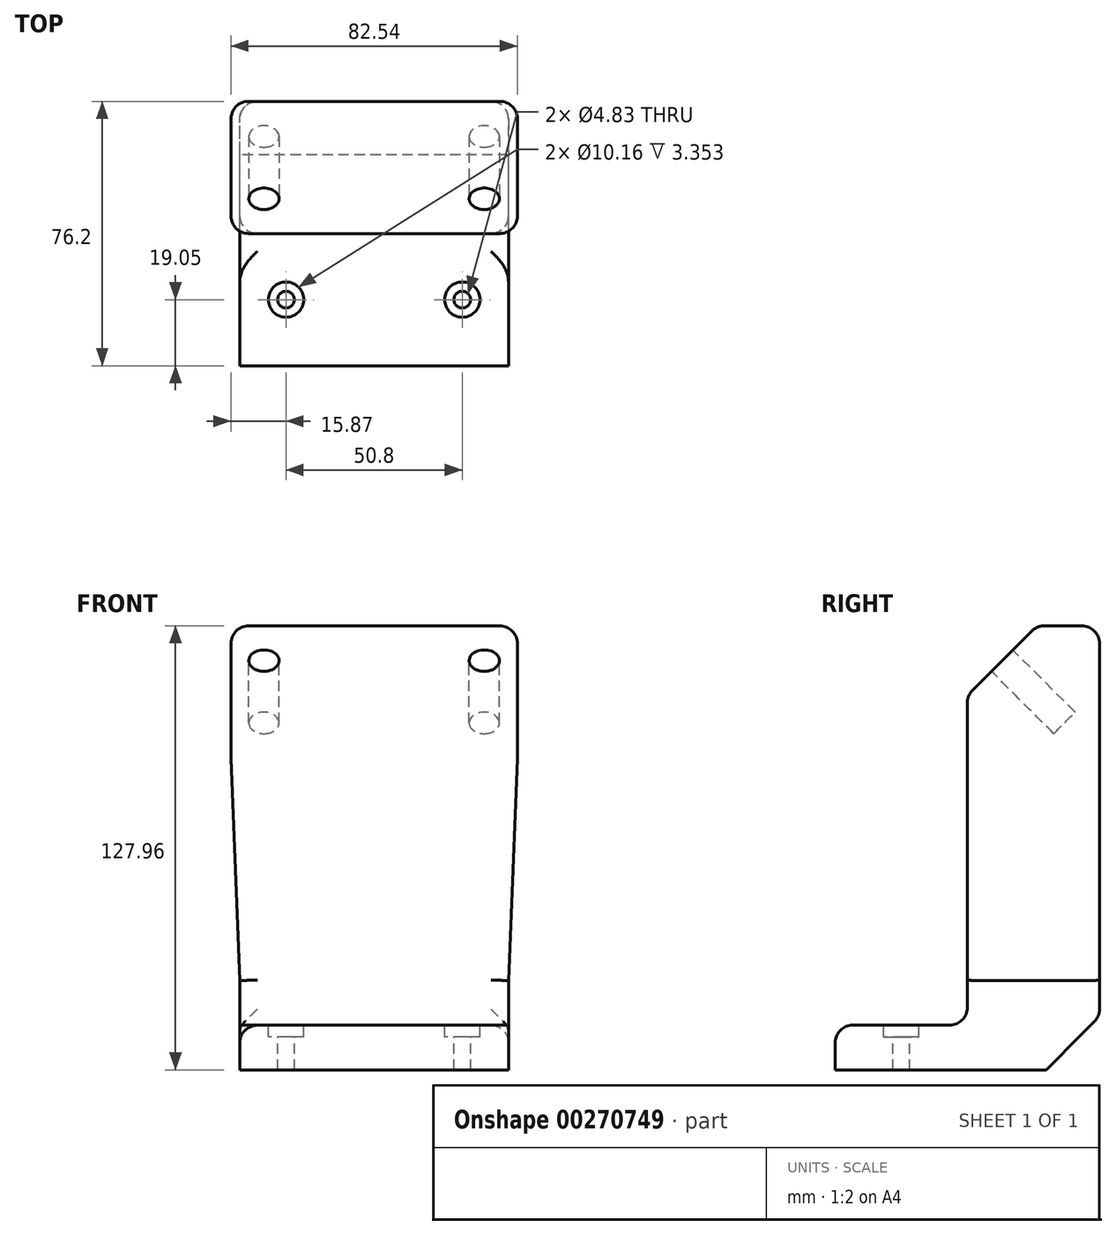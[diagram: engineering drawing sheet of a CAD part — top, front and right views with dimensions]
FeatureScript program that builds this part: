
annotation { "Feature Type Name" : "Feature", "Feature Type Description" : "" }
export const myFeature = defineFeature(function(context is Context, id is Id, definition is map)
    precondition{}
    {
        {
            var Q0;
            Q0=qCreatedBy(makeId("Front.planeOp"),FACE);
            var sketch = newSketch(context, id + "F0", { "sketchPlane" : qUnion([Q0])});
            skLineSegment(sketch, "E0.top", {"start": v(0, -76.68) * mm, "end": v(-38.71, -76.68) * mm});
            skLineSegment(sketch, "E0.left", {"start": v(41.28, 51.28) * mm, "end": v(41.28, 13.06) * mm});
            skLineSegment(sketch, "E0.right", {"start": v(-41.27, 51.28) * mm, "end": v(-41.28, 13.06) * mm});
            skPoint(sketch, "E0.middle", {"position": v(0, 0) * mm});
            skLineSegment(sketch, "E1", {"start": v(-38.74, -50.4) * mm, "end": v(-41.28, 13.06) * mm});
            skPoint(sketch, "E2.endSnap0", {"position": v(0, -76.68) * mm});
            skPoint(sketch, "E3.orphan", {"position": v(-41.28, -76.68) * mm});
            skPoint(sketch, "E2.end.orphan", {"position": v(0, -57.6) * mm});
            skPoint(sketch, "E2.start.orphan", {"position": v(0, -76.68) * mm});
            skPoint(sketch, "E4.orphan", {"position": v(41.28, -76.68) * mm});
            skLineSegment(sketch, "E5", {"start": v(-41.27, 13.06) * mm, "end": v(-38.71, -50.93) * mm});
            skLineSegment(sketch, "E6", {"start": v(-38.71, -50.93) * mm, "end": v(-38.71, -76.68) * mm});
            skLineSegment(sketch, "E7", {"start": v(0, -76.68) * mm, "end": v(0, -57.6) * mm});
            skLineSegment(sketch, "E8.MirrorCS", {"start": v(0, -76.68) * mm, "end": v(38.71, -76.68) * mm});
            skLineSegment(sketch, "E9.MirrorCS", {"start": v(38.71, -50.93) * mm, "end": v(38.71, -76.68) * mm});
            skLineSegment(sketch, "E10.MirrorCS", {"start": v(41.28, 13.06) * mm, "end": v(38.71, -50.93) * mm});
            skPoint(sketch, "E0.bottom.end.orphan", {"position": v(-41.27, 76.68) * mm});
            skPoint(sketch, "E11.orphan", {"position": v(41.28, 76.68) * mm});
            skLineSegment(sketch, "E12", {"start": v(41.28, 51.28) * mm, "end": v(-41.28, 51.28) * mm});
            skSolve(sketch);
        }
        {
            var Q0;
            Q0 = qSketchRegion(id + "F0", true);
            extrude(context, id + "F1", {"entities" : qUnion([Q0]), "depth" : 38.1 * mm});
        }
        {
            var Q0;
            Q0=makeQuery(id+"F1.opExtrude","SWEPT_FACE",FACE,{"disambiguationData":[OSD([sQuery(id+"F0.wireOp",EDGE,"E0.left")])]});
            var sketch = newSketch(context, id + "F2", { "sketchPlane" : qUnion([Q0])});
            skLineSegment(sketch, "E13", {"start": v(-18.08, 51.28) * mm, "end": v(-38.1, 51.28) * mm});
            skLineSegment(sketch, "E14", {"start": v(-38.1, 51.28) * mm, "end": v(-38.1, 31.27) * mm});
            skLineSegment(sketch, "E15", {"start": v(-18.08, 51.28) * mm, "end": v(-38.1, 31.27) * mm});
            skSolve(sketch);
        }
        {
            var Q0;
            Q0 = qSketchRegion(id + "F2", true);
            extrude(context, id + "F3", {"entities" : qUnion([Q0]), "operationType" : NewBodyOperationType.REMOVE, "oppositeDirection" : true, "depth" : 127 * mm});
        }
        {
            var Q0;
            Q0=makeQuery(id+"F3.boolean.opBoolean","COPY",FACE,{"derivedFrom":makeQuery(id+"F3.opExtrude","SWEPT_FACE",FACE,{"disambiguationData":[OSD([sQuery(id+"F2.wireOp",EDGE,"E15")])]})});
            var sketch = newSketch(context, id + "F4", { "sketchPlane" : qUnion([Q0])});
            skPoint(sketch, "E16", {"position": v(-31.75, 18.3) * mm});
            skPoint(sketch, "E17", {"position": v(31.75, 18.3) * mm});
            skPoint(sketch, "E18", {"position": v(-31.75, 9.32) * mm});
            skPoint(sketch, "E18.positionSnap0", {"position": v(-41.28, 9.32) * mm});
            skPoint(sketch, "E19", {"position": v(31.75, 9.32) * mm});
            skCircle(sketch, "E20", {"center": v(-31.75, 9.32) * mm, "radius": 4.37 * mm});
            skCircle(sketch, "E21", {"center": v(31.75, 9.32) * mm, "radius": 4.37 * mm});
            skSolve(sketch);
        }
        {
            var Q0;
            Q0 = qSketchRegion(id + "F4", true);
            extrude(context, id + "F5", {"entities" : qUnion([Q0]), "operationType" : NewBodyOperationType.REMOVE, "oppositeDirection" : true, "depth" : 25.4 * mm});
        }
        {
            var Q0;
            Q0=makeQuery(id+"F1.opExtrude","CAP_FACE",FACE,{"disambiguationData":[OSD([sQuery(id+"F0.wireOp",EDGE,"E0.bottom"),sQuery(id+"F0.wireOp",EDGE,"E0.top"),sQuery(id+"F0.wireOp",EDGE,"E0.left"),sQuery(id+"F0.wireOp",EDGE,"E0.right"),sQuery(id+"F0.wireOp",EDGE,"E5"),sQuery(id+"F0.wireOp",EDGE,"E6"),sQuery(id+"F0.wireOp",EDGE,"E8.MirrorCS"),sQuery(id+"F0.wireOp",EDGE,"E9.MirrorCS"),sQuery(id+"F0.wireOp",EDGE,"E10.MirrorCS")])],"isStart":false});
            var sketch = newSketch(context, id + "F6", { "sketchPlane" : qUnion([Q0])});
            skLineSegment(sketch, "E22.bottom", {"start": v(38.71, -76.68) * mm, "end": v(-38.71, -76.68) * mm});
            skLineSegment(sketch, "E22.left", {"start": v(38.71, -76.68) * mm, "end": v(38.71, -63.8) * mm});
            skLineSegment(sketch, "E22.right", {"start": v(-38.71, -76.68) * mm, "end": v(-38.71, -63.8) * mm});
            skPoint(sketch, "E22.middle", {"position": v(0, -67.48) * mm});
            skPoint(sketch, "E22.middle.positionSnap0", {"position": v(0, -76.68) * mm});
            skPoint(sketch, "E22.centerSnap0", {"position": v(0, -76.68) * mm});
            skLineSegment(sketch, "E23", {"start": v(-38.71, -63.8) * mm, "end": v(38.71, -63.8) * mm});
            skPoint(sketch, "E24.orphan", {"position": v(38.71, -58.28) * mm});
            skPoint(sketch, "E25.orphan", {"position": v(-38.71, -58.28) * mm});
            skSolve(sketch);
        }
        {
            var Q0;
            Q0 = qSketchRegion(id + "F6", true);
            extrude(context, id + "F7", {"entities" : qUnion([Q0]), "operationType" : NewBodyOperationType.ADD, "depth" : 38.1 * mm});
        }
        {
            var Q0;
            Q0=makeQuery(id+"F7.opExtrude","SWEPT_FACE",FACE,{"disambiguationData":[OSD([sQuery(id+"F6.wireOp",EDGE,"E23")])]});
            var sketch = newSketch(context, id + "F8", { "sketchPlane" : qUnion([Q0])});
            skLineSegment(sketch, "E26", {"start": v(0, -57.15) * mm, "end": v(-25.4, -57.15) * mm});
            skPoint(sketch, "E26.startSnap0", {"position": v(-38.71, -57.15) * mm});
            skPoint(sketch, "E26.endSnap0", {"position": v(38.71, -57.15) * mm});
            skLineSegment(sketch, "E27", {"start": v(-25.4, -57.15) * mm, "end": v(25.4, -57.15) * mm});
            skPoint(sketch, "E28", {"position": v(-25.4, -57.15) * mm});
            skPoint(sketch, "E29", {"position": v(25.4, -57.15) * mm});
            skSolve(sketch);
        }
        {
            var Q0;
            Q0=sQuery(id+"F8.wireOp",VERTEX,"E28");
            var Q1;
            Q1=sQuery(id+"F8.wireOp",VERTEX,"E29");
            var Q2;
            Q2=makeQuery(id+"F1.opExtrude","SWEPT_BODY",BODY,{"disambiguationData":[OSD([sQuery(id+"F0.wireOp",EDGE,"E0.bottom"),sQuery(id+"F0.wireOp",EDGE,"E0.top"),sQuery(id+"F0.wireOp",EDGE,"E0.left"),sQuery(id+"F0.wireOp",EDGE,"E0.right"),sQuery(id+"F0.wireOp",EDGE,"E5"),sQuery(id+"F0.wireOp",EDGE,"E6"),sQuery(id+"F0.wireOp",EDGE,"E8.MirrorCS"),sQuery(id+"F0.wireOp",EDGE,"E9.MirrorCS"),sQuery(id+"F0.wireOp",EDGE,"E10.MirrorCS")])]});
            hole(context, id + "F9", {"style" : HoleStyle.C_BORE, "endStyle" : HoleEndStyle.THROUGH, "holeDiameter" : 4.83 * mm, "cBoreDiameter" : 10.16 * mm, "cBoreDepth" : 3.35 * mm, "tappedDepth" : 12.7 * mm, "tapClearance" : 3, "locations" : qUnion([Q0, Q1]), "scope" : qUnion([Q2])});
        }
        {
            var Q0;
            Q0=makeQuery(id+"F7.boolean.opBoolean","MERGE",FACE,{"derivedFrom":[makeQuery(id+"F1.opExtrude","SWEPT_FACE",FACE,{"disambiguationData":[OSD([sQuery(id+"F0.wireOp",EDGE,"E6")])]}),makeQuery(id+"F7.opExtrude","SWEPT_FACE",FACE,{"disambiguationData":[OSD([sQuery(id+"F6.wireOp",EDGE,"E22.right")])]})]});
            var sketch = newSketch(context, id + "F10", { "sketchPlane" : qUnion([Q0])});
            skLineSegment(sketch, "E30", {"start": v(0, -76.68) * mm, "end": v(0, -63.8) * mm});
            skLineSegment(sketch, "E31", {"start": v(0, -76.68) * mm, "end": v(12.88, -76.68) * mm});
            skLineSegment(sketch, "E32", {"start": v(12.88, -76.68) * mm, "end": v(0, -63.8) * mm});
            skSolve(sketch);
        }
        {
            var Q0;
            Q0 = qSketchRegion(id + "F10", true);
            extrude(context, id + "F11", {"entities" : qUnion([Q0]), "operationType" : NewBodyOperationType.REMOVE, "oppositeDirection" : true, "depth" : 127 * mm});
        }
        {
            var Q0;
            Q0=makeQuery(id+"F7.boolean.opBoolean","MERGE",FACE,{"derivedFrom":[makeQuery(id+"F1.opExtrude","SWEPT_FACE",FACE,{"disambiguationData":[OSD([sQuery(id+"F0.wireOp",EDGE,"E6")])]}),makeQuery(id+"F7.opExtrude","SWEPT_FACE",FACE,{"disambiguationData":[OSD([sQuery(id+"F6.wireOp",EDGE,"E22.right")])]})]});
            var sketch = newSketch(context, id + "F12", { "sketchPlane" : qUnion([Q0])});
            skLineSegment(sketch, "E33", {"start": v(0, -63.8) * mm, "end": v(0, -61.26) * mm});
            skLineSegment(sketch, "E34", {"start": v(12.88, -76.68) * mm, "end": v(15.42, -76.68) * mm});
            skLineSegment(sketch, "E35", {"start": v(15.42, -76.68) * mm, "end": v(0, -61.26) * mm});
            skLineSegment(sketch, "E36", {"start": v(0, -63.8) * mm, "end": v(12.88, -76.68) * mm});
            skSolve(sketch);
        }
        {
            var Q0;
            Q0 = qSketchRegion(id + "F12", true);
            extrude(context, id + "F13", {"entities" : qUnion([Q0]), "operationType" : NewBodyOperationType.REMOVE, "oppositeDirection" : true, "depth" : 127 * mm});
        }
        {
            var Q0;
            Q0=makeQuery(id+"F7.opExtrude","CAP_EDGE",EDGE,{"disambiguationData":[OSD([sQuery(id+"F6.wireOp",EDGE,"E23")])],"isStart":true});
            var Q1;
            Q1=makeQuery(id+"F13.boolean.opBoolean","COPY",EDGE,{"derivedFrom":makeQuery(id+"F13.opExtrude","SWEPT_EDGE",EDGE,{"disambiguationData":[OSD([sQuery(id+"F0.wireOp",EDGE,"E6"),sQuery(id+"F12.wireOp",EDGE,"E33"),sQuery(id+"F12.wireOp",EDGE,"E35")])]})});
            var Q2;
            Q2=makeQuery(id+"F1.opExtrude","CAP_EDGE",EDGE,{"disambiguationData":[OSD([sQuery(id+"F0.wireOp",EDGE,"E0.bottom")])],"isStart":true});
            var Q3;
            Q3=makeQuery(id+"F7.opExtrude","CAP_EDGE",EDGE,{"disambiguationData":[OSD([sQuery(id+"F6.wireOp",EDGE,"E23")])],"isStart":false});
            var Q4;
            Q4=makeQuery(id+"F1.opExtrude","CAP_FACE",FACE,{"disambiguationData":[OSD([sQuery(id+"F0.wireOp",EDGE,"E0.top"),sQuery(id+"F0.wireOp",EDGE,"E0.left"),sQuery(id+"F0.wireOp",EDGE,"E0.right"),sQuery(id+"F0.wireOp",EDGE,"E5"),sQuery(id+"F0.wireOp",EDGE,"E6"),sQuery(id+"F0.wireOp",EDGE,"E8.MirrorCS"),sQuery(id+"F0.wireOp",EDGE,"E9.MirrorCS"),sQuery(id+"F0.wireOp",EDGE,"E10.MirrorCS"),sQuery(id+"F0.wireOp",EDGE,"E12")])],"isStart":false});
            var Q5;
            Q5=makeQuery(id+"F1.opExtrude","CAP_FACE",FACE,{"disambiguationData":[OSD([sQuery(id+"F0.wireOp",EDGE,"E0.top"),sQuery(id+"F0.wireOp",EDGE,"E0.left"),sQuery(id+"F0.wireOp",EDGE,"E0.right"),sQuery(id+"F0.wireOp",EDGE,"E5"),sQuery(id+"F0.wireOp",EDGE,"E6"),sQuery(id+"F0.wireOp",EDGE,"E8.MirrorCS"),sQuery(id+"F0.wireOp",EDGE,"E9.MirrorCS"),sQuery(id+"F0.wireOp",EDGE,"E10.MirrorCS"),sQuery(id+"F0.wireOp",EDGE,"E12")])],"isStart":true});
            var Q6;
            Q6=makeQuery(id+"F1.opExtrude","SWEPT_FACE",FACE,{"disambiguationData":[OSD([sQuery(id+"F0.wireOp",EDGE,"E12")])]});
            var Q7;
            Q7=makeQuery(id+"F1.opExtrude","SWEPT_FACE",FACE,{"disambiguationData":[OSD([sQuery(id+"F0.wireOp",EDGE,"E0.left")])]});
            var Q8;
            Q8=makeQuery(id+"F1.opExtrude","SWEPT_FACE",FACE,{"disambiguationData":[OSD([sQuery(id+"F0.wireOp",EDGE,"E0.right")])]});
            fillet(context, id + "F14", {"entities" : qUnion([Q0, Q1, Q2, Q3, Q4, Q5, Q6, Q7, Q8]), "radius" : 5.08 * mm, "tangentPropagation" : true, "allowEdgeOverflow" : false});
        }
    });
